SOLIDWORKS PART (.sldprt)
format: sldprt  version: not decoded by parser v0  size: 187,392 bytes
history: native  units: mm
features: plane x5, sketch x5, extrude x5, fillet x4, material x1 (+10 scaffold rows collapsed)
feature tree (30):
  scaffold x10  (default folders/planes/origin — collapsed)
  material  "Matériau <non spécifié>"
  plane  "Plan de face"
  plane  "Plan de dessus"
  plane  "Plan de droite"
  sketch  "Esquisse1"
  extrude  "Extrusion1"  Depth=5mm
  sketch  "Esquisse2"  dims[D1=2.1mm]
  extrude  "Extrusion2"  Depth=1.9mm
  sketch  "Esquisse4"  dims[D1=~0.282484mm]
  extrude  "Extrusion3"  Depth=2mm
  plane  "Plan1"  Offset=0.01mm
  sketch  "Esquisse6"  dims[D1=~1.408708mm]
  extrude  "Extrusion5"  Depth=1mm
  plane  "Plan2"  Offset=0.01mm
  sketch  "Esquisse7"  dims[D1=0.1mm D2=0.1mm D3=0.45mm D4=0.9mm D5=0.45mm D6=0.9mm D7=0.2mm D8=0.1mm D9=0.1mm]
  extrude  "Extrusion6"  Depth=3mm
  fillet  "Congé1"  Radius=0.45mm
  fillet  "Congé2"  Radius=0.45mm
  fillet  "Congé3"  Radius=0.45mm
  fillet  "Congé4"  Radius=0.45mm
decode coverage: 13 of 14 modeling features carry decoded parameters
note: ~ marks probable driven/reference dimensions
note: suppression state not decoded; provenance and decode notes live in map.json
